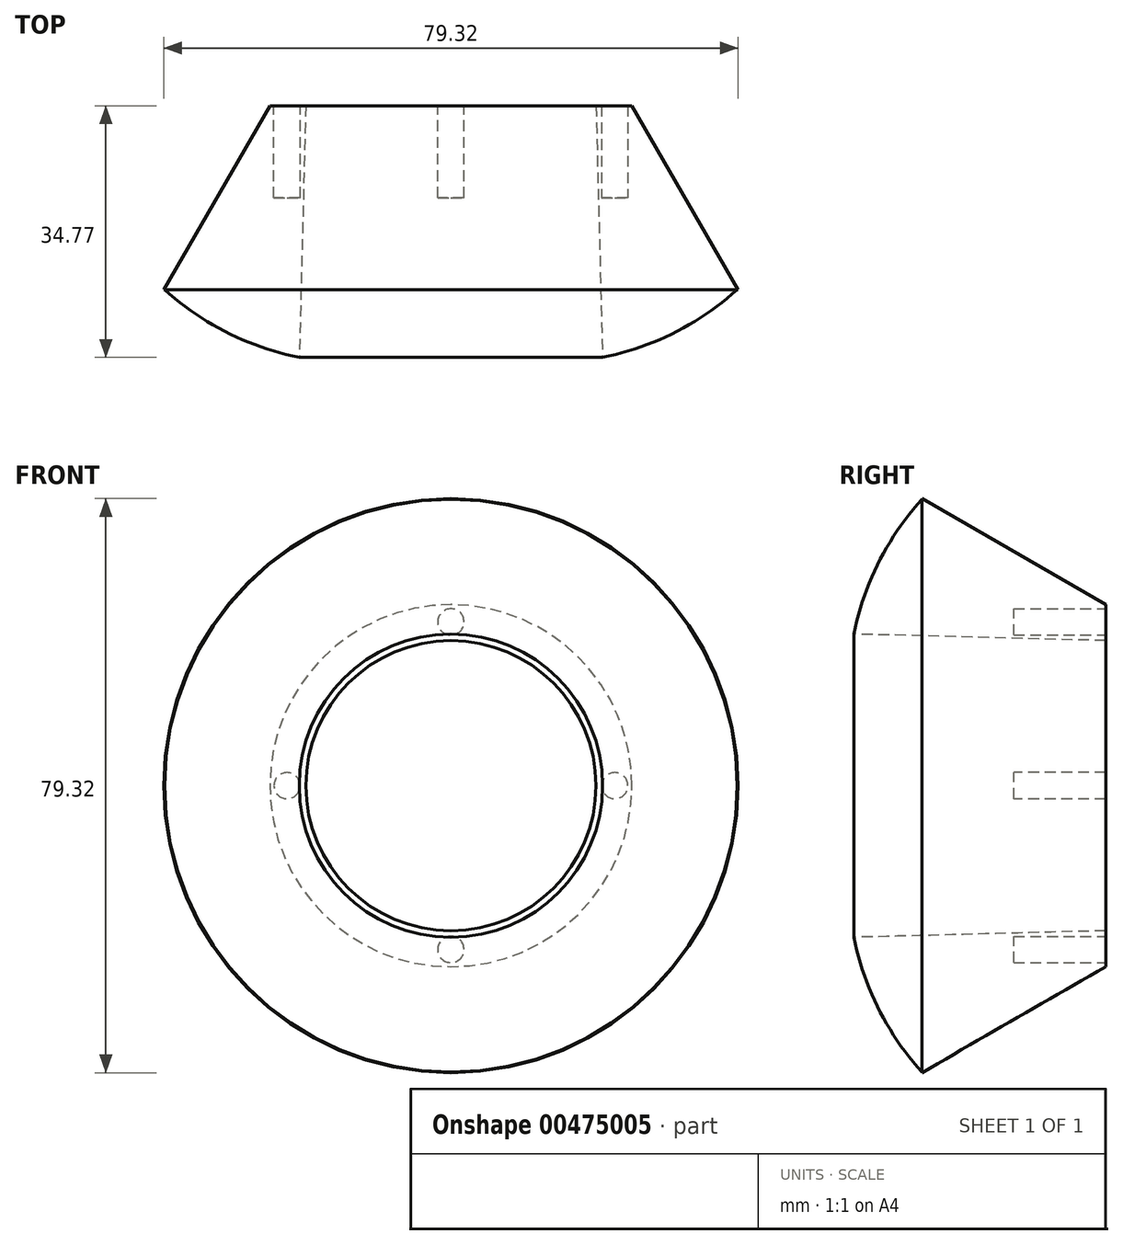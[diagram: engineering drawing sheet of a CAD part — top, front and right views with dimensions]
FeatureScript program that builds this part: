
annotation { "Feature Type Name" : "Feature", "Feature Type Description" : "" }
export const myFeature = defineFeature(function(context is Context, id is Id, definition is map)
    precondition{}
    {
        {
            var Q0;
            Q0=qCreatedBy(makeId("Front.planeOp"),FACE);
            var sketch = newSketch(context, id + "F0", { "sketchPlane" : qUnion([Q0])});
            skCircle(sketch, "E0", {"center": v(0, 0) * mm, "radius": 25 * mm});
            skSolve(sketch);
        }
        {
            var Q0;
            Q0=makeQuery(id+"F0.imprint","IMPRINT",FACE,{"disambiguationData":[TD([[makeQuery(id+"F0.imprint","IMPRINT",EDGE,{"derivedFrom":sQuery(id+"F0.wireOp",EDGE,"E0")}),1.0]])]});
            extrude(context, id + "F1", {"entities" : qUnion([Q0]), "depth" : 25.4 * mm, "hasDraft" : true, "draftAngle" : 30 * degree});
        }
        {
            var Q0;
            Q0=qCreatedBy(makeId("Front.planeOp"),FACE);
            cPlane(context, id + "F2", {"entities" : qUnion([Q0]), "cplaneType" : CPlaneType.OFFSET, "offset" : 25.4 * mm, "width" : 152.4 * mm, "height" : 152.4 * mm});
        }
        {
            var Q0;
            Q0=qCreatedBy(id+"F2.planeOp",FACE);
            var sketch = newSketch(context, id + "F3", { "sketchPlane" : qUnion([Q0])});
            skCircle(sketch, "E1", {"center": v(0, 0) * mm, "radius": 39.55 * mm});
            skSolve(sketch);
        }
        {
            var Q0;
            Q0=makeQuery(id+"F3.imprint","IMPRINT",FACE,{"disambiguationData":[TD([[makeQuery(id+"F3.imprint","IMPRINT",EDGE,{"derivedFrom":sQuery(id+"F3.wireOp",EDGE,"E1")}),1.0]])]});
            extrude(context, id + "F4", {"entities" : qUnion([Q0]), "operationType" : NewBodyOperationType.ADD, "depth" : 10.16 * mm});
        }
        {
            var Q0;
            Q0=makeQuery(id+"F4.opExtrude","CAP_EDGE",EDGE,{"disambiguationData":[OSD([sQuery(id+"F3.wireOp",EDGE,"E1")])],"isStart":false});
            fillet(context, id + "F5", {"entities" : qUnion([Q0]), "radius" : 39.5 * mm, "tangentPropagation" : true, "allowEdgeOverflow" : false});
        }
        {
            var Q0;
            Q0=qCreatedBy(makeId("Front.planeOp"),FACE);
            var sketch = newSketch(context, id + "F6", { "sketchPlane" : qUnion([Q0])});
            skCircle(sketch, "E2", {"center": v(0, 0) * mm, "radius": 20.04 * mm});
            skSolve(sketch);
        }
        {
            var Q0;
            Q0=makeQuery(id+"F6.imprint","IMPRINT",FACE,{"disambiguationData":[TD([[makeQuery(id+"F6.imprint","IMPRINT",EDGE,{"derivedFrom":sQuery(id+"F6.wireOp",EDGE,"E2")}),1.0]])]});
            var Q1;
            Q1=sQuery(id+"F6.wireOp",EDGE,"E2");
            extrude(context, id + "F7", {"entities" : qUnion([Q0]), "operationType" : NewBodyOperationType.REMOVE, "surfaceEntities" : qUnion([Q1]), "endBound" : BoundingType.THROUGH_ALL, "depth" : 25.4 * mm, "hasDraft" : true, "draftAngle" : 1.5 * degree});
        }
        {
            var Q0;
            Q0=qCreatedBy(makeId("Front.planeOp"),FACE);
            var sketch = newSketch(context, id + "F8", { "sketchPlane" : qUnion([Q0])});
            skCircle(sketch, "E3", {"center": v(0, 22.63) * mm, "radius": 1.81 * mm});
            skCircle(sketch, "E4", {"center": v(22.63, 0) * mm, "radius": 1.82 * mm});
            skCircle(sketch, "E5", {"center": v(0, -22.63) * mm, "radius": 1.82 * mm});
            skCircle(sketch, "E6", {"center": v(-22.63, 0) * mm, "radius": 1.82 * mm});
            skSolve(sketch);
        }
        {
            var Q0;
            Q0=makeQuery(id+"F8.imprint","IMPRINT",FACE,{"disambiguationData":[TD([[makeQuery(id+"F8.imprint","IMPRINT",EDGE,{"derivedFrom":sQuery(id+"F8.wireOp",EDGE,"E3")}),1.0]])]});
            var Q1;
            Q1=sQuery(id+"F8.wireOp",EDGE,"E3");
            extrude(context, id + "F9", {"entities" : qUnion([Q0]), "operationType" : NewBodyOperationType.REMOVE, "surfaceEntities" : qUnion([Q1]), "depth" : 12.7 * mm, "hasSecondDirection" : true, "secondDirectionOppositeDirection" : true, "secondDirectionDepth" : 25.4 * mm});
        }
        {
            var Q0;
            Q0=makeQuery(id+"F8.imprint","IMPRINT",FACE,{"disambiguationData":[TD([[makeQuery(id+"F8.imprint","IMPRINT",EDGE,{"derivedFrom":sQuery(id+"F8.wireOp",EDGE,"E4")}),1.0]])]});
            var Q1;
            Q1=sQuery(id+"F8.wireOp",EDGE,"E4");
            extrude(context, id + "F10", {"entities" : qUnion([Q0]), "operationType" : NewBodyOperationType.REMOVE, "surfaceEntities" : qUnion([Q1]), "oppositeDirection" : true, "depth" : 12.7 * mm, "hasSecondDirection" : true, "secondDirectionOppositeDirection" : false, "secondDirectionDepth" : 12.7 * mm});
        }
        {
            var Q0;
            Q0 = qSketchRegion(id + "F8", true);
            var Q1;
            Q1=sQuery(id+"F8.wireOp",EDGE,"E5");
            extrude(context, id + "F11", {"entities" : qUnion([Q0]), "operationType" : NewBodyOperationType.REMOVE, "surfaceEntities" : qUnion([Q1]), "depth" : 12.7 * mm});
        }
    });
